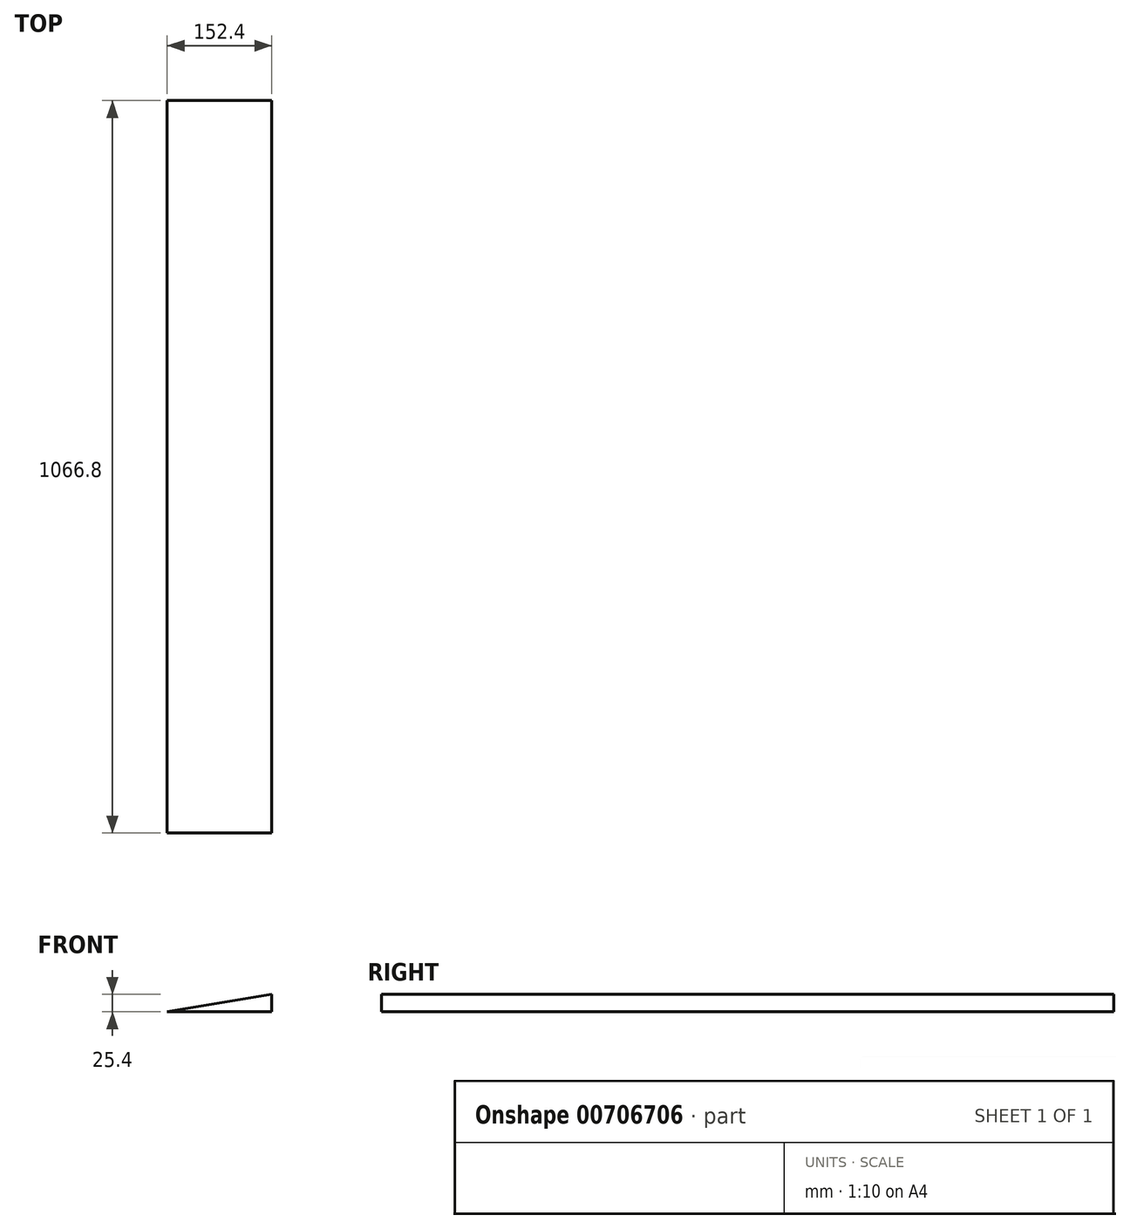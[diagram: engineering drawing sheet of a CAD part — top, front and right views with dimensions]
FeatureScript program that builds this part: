
annotation { "Feature Type Name" : "Feature", "Feature Type Description" : "" }
export const myFeature = defineFeature(function(context is Context, id is Id, definition is map)
    precondition{}
    {
        {
            var Q0;
            Q0=qCreatedBy(makeId("Front.planeOp"),FACE);
            var sketch = newSketch(context, id + "F0", { "sketchPlane" : qUnion([Q0])});
            skLineSegment(sketch, "E0", {"start": v(0, 0) * mm, "end": v(152.4, 0) * mm});
            skLineSegment(sketch, "E1", {"start": v(152.4, 0) * mm, "end": v(152.4, 25.4) * mm});
            skLineSegment(sketch, "E2", {"start": v(152.4, 25.4) * mm, "end": v(0, 0) * mm});
            skSolve(sketch);
        }
        {
            var Q0;
            Q0=makeQuery(id+"F0.imprint","IMPRINT",FACE,{"disambiguationData":[TD([[makeQuery(id+"F0.imprint","IMPRINT",EDGE,{"derivedFrom":sQuery(id+"F0.wireOp",EDGE,"E0")}),1.0]])]});
            extrude(context, id + "F1", {"entities" : qUnion([Q0]), "depth" : 1066.8 * mm, "offsetDistance" : 25.4 * mm});
        }
    });
